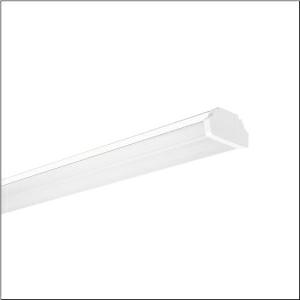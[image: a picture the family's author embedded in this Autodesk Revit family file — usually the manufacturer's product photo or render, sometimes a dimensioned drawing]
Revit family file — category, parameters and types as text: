
# Revit family: dus_r__31_gen_2_53bd812mv4fxd2_6b37
name_source: partatom
category: Lighting Fixtures
units: mm (PartAtom-declared; Revit-internal decimal feet)

## family parameters
Cut with Voids When Loaded = No
Host = Face
Light Source = No
Part Type = Normal
Room Calculation Point = No
Round Connector Dimension = Use Diameter
Shared = No

## types (1)
- --- (1 x LED, 15440 lm, 82.3 W, 4000K)
    Apparent Load = 82 VA
    CIE Flux Codes = 47 80 95 93 100
    Color Rendering = 80
    Color Temperature = 4000K
    Default Elevation = 1800 mm
    Description = DUS® 31 Gen.2, luminaire insert, of sheet steel, coil coated, white, length: 1.535mm, width: 81mm, height: 90mm, 5x system unit, system units: 307mm, LED rated luminous flux: 15.440lm, light colour: 840, control gear: ON/OFF Multilumen, control gear: ECG, with plug, 3-pole, with phase selection, mains connection: 220..240V, AC, 50/60Hz, rated input power: 82W, through-wiring accessed according to module size, primary optical cover: cover, of PMMA, light emission: direct distribution, primary light characteristic: symmetric, protection rating (complete): IP20, protection rating (LED compartment): IP50, insulation class (complete): insulation class I (protective earthing), certification: CE, ENEC, VDE, UKCA, impact resistance: IK03, permissible ambient temperature for indoor applications: -35..+35°C, corresponds to IFS (International Featured Standards) requirements for safety and quality in the food industry, reducing of maximum allowable ambient temperature of 5°C with ceiling mounting, packaging unit: 1 piece
    Height = 95 mm
    Lamp = 1 x LED
    Lamp Light Flux = 15440 lm
    Lamp Power = 82.3 W
    Lamp count = 1
    Length = 1535 mm
    Luminous efficacy = 188 lm/W
    Manufacturer = Siteco
    ModVariant = No
    Model = 53BD812MV4FXD2
    Mounting Place = Ceiling
    Mounting Type = Pendant
    Number of Poles = 1
    OnlyDefault = Yes
    Power Factor = 1
    Product Name = DUS® 31 Gen.2
    Product group = luminaire insert
    ProductGroupID = 901
    Protection Class = Protection class I
    Protection Degree = IP 20
    RLX_Detail_Level = 1
    RLX_Emergency_Light_Flux = 0 lm
    RLX_Emergency_Type = 0
    RLX_Emergency_Type_DB = No
    RlxData = <blob elided: 29793 chars, md5=e634754b>
    Socket = socket
    Standby Power = 0 W
    System Light Flux = 15440 lm
    System Power = 82 W
    Type Comments = factory setting: luminous flux: 100 % | (A | C | E) | 193 mA
    Type Image = l_1319596.jpg
    URL = http://relux.com
    VarID = @adj_010051
    Voltage = 0 V
    Weight = 0.00 kg
    Width = 81 mm

## geometry (parser evidence)
native form markers: Blend x4, Sweep x12
no freeform markers — native parametric forms only
